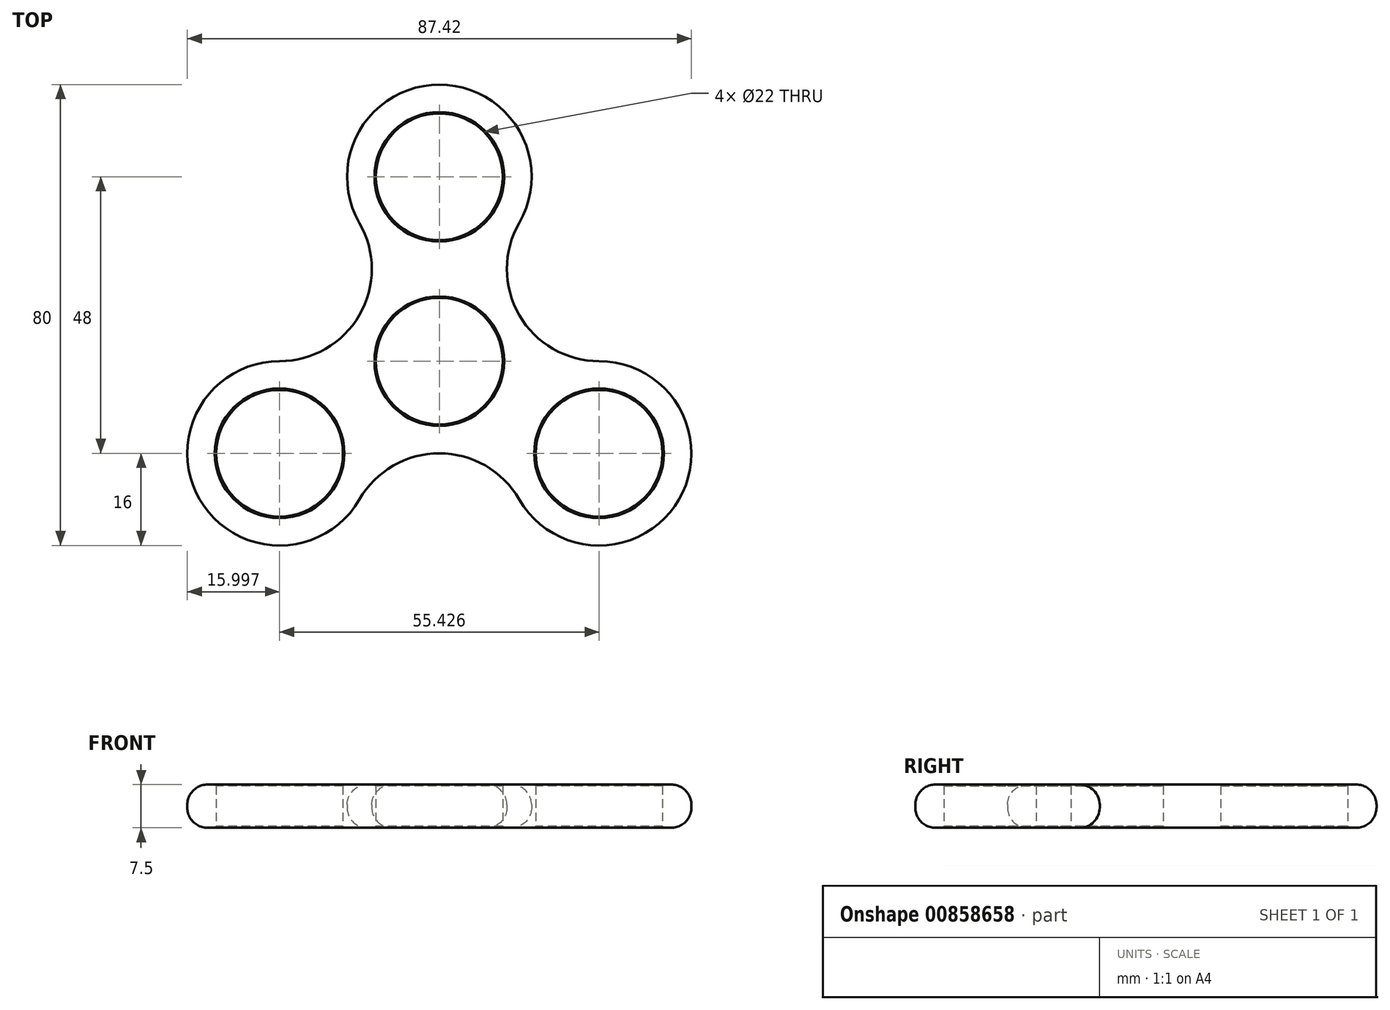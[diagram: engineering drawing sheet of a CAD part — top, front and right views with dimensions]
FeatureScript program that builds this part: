
annotation { "Feature Type Name" : "Feature", "Feature Type Description" : "" }
export const myFeature = defineFeature(function(context is Context, id is Id, definition is map)
    precondition{}
    {
        {
            var Q0;
            Q0=qCreatedBy(makeId("Top.planeOp"),FACE);
            var sketch = newSketch(context, id + "F0", { "sketchPlane" : qUnion([Q0])});
            skCircle(sketch, "E0", {"center": v(0, 0) * mm, "radius": 11 * mm});
            skLineSegment(sketch, "E1", {"start": v(0, 0) * mm, "end": v(0, 21) * mm});
            skLineSegment(sketch, "E2", {"start": v(0, 21) * mm, "end": v(0, 32) * mm});
            skCircle(sketch, "E3", {"center": v(0, 32) * mm, "radius": 11 * mm});
            skArc(sketch, "E4", {"start": v(13.86, 24) * mm, "mid": v(0, 48) * mm, "end": v(-13.86, 24) * mm});
            skArc(sketch, "E5.1.0", {"start": v(-27.71, 0) * mm, "mid": v(-41.57, -24) * mm, "end": v(-13.86, -24) * mm});
            skCircle(sketch, "E5.1.1", {"center": v(-27.71, -16) * mm, "radius": 11 * mm});
            skArc(sketch, "E5.2.0", {"start": v(13.86, -24) * mm, "mid": v(41.57, -24) * mm, "end": v(27.71, 0) * mm});
            skCircle(sketch, "E5.2.1", {"center": v(27.71, -16) * mm, "radius": 11 * mm});
            skArc(sketch, "E6", {"start": v(13.86, 24) * mm, "mid": v(13.86, 8) * mm, "end": v(27.71, 0) * mm});
            skArc(sketch, "E7.1.0", {"start": v(-27.71, 0) * mm, "mid": v(-13.86, 8) * mm, "end": v(-13.86, 24) * mm});
            skArc(sketch, "E7.2.0", {"start": v(13.86, -24) * mm, "mid": v(0, -16) * mm, "end": v(-13.86, -24) * mm});
            skSolve(sketch);
        }
        {
            var Q0;
            Q0=makeQuery(id+"F0.imprint","IMPRINT",FACE,{"disambiguationData":[TD([[makeQuery(id+"F0.imprint","IMPRINT",EDGE,{"derivedFrom":sQuery(id+"F0.wireOp",EDGE,"E0")}),-1.0]])]});
            extrude(context, id + "F1", {"entities" : qUnion([Q0]), "depth" : 7.5 * mm, "offsetDistance" : 25 * mm});
        }
        {
            var Q0;
            Q0=makeQuery(id+"F1.opExtrude","CAP_EDGE",EDGE,{"disambiguationData":[OSD([sQuery(id+"F0.wireOp",EDGE,"E5.1.0")])],"isStart":false});
            var Q1;
            Q1=makeQuery(id+"F1.opExtrude","CAP_EDGE",EDGE,{"disambiguationData":[OSD([sQuery(id+"F0.wireOp",EDGE,"E7.2.0")])],"isStart":true});
            fillet(context, id + "F2", {"entities" : qUnion([Q0, Q1]), "radius" : 3.5 * mm, "tangentPropagation" : true, "allowEdgeOverflow" : false});
        }
        {
            var Q0;
            Q0=makeQuery(id+"F1.opExtrude","CAP_EDGE",EDGE,{"disambiguationData":[OSD([sQuery(id+"F0.wireOp",EDGE,"E3")])],"isStart":false});
            var Q1;
            Q1=makeQuery(id+"F1.opExtrude","CAP_EDGE",EDGE,{"disambiguationData":[OSD([sQuery(id+"F0.wireOp",EDGE,"E0")])],"isStart":false});
            var Q2;
            Q2=makeQuery(id+"F1.opExtrude","CAP_EDGE",EDGE,{"disambiguationData":[OSD([sQuery(id+"F0.wireOp",EDGE,"E5.1.1")])],"isStart":false});
            var Q3;
            Q3=makeQuery(id+"F1.opExtrude","CAP_EDGE",EDGE,{"disambiguationData":[OSD([sQuery(id+"F0.wireOp",EDGE,"E5.2.1")])],"isStart":false});
            var Q4;
            Q4=makeQuery(id+"F1.opExtrude","CAP_EDGE",EDGE,{"disambiguationData":[OSD([sQuery(id+"F0.wireOp",EDGE,"E5.2.1")])],"isStart":true});
            var Q5;
            Q5=makeQuery(id+"F1.opExtrude","CAP_EDGE",EDGE,{"disambiguationData":[OSD([sQuery(id+"F0.wireOp",EDGE,"E0")])],"isStart":true});
            var Q6;
            Q6=makeQuery(id+"F1.opExtrude","CAP_EDGE",EDGE,{"disambiguationData":[OSD([sQuery(id+"F0.wireOp",EDGE,"E5.1.1")])],"isStart":true});
            var Q7;
            Q7=makeQuery(id+"F1.opExtrude","CAP_EDGE",EDGE,{"disambiguationData":[OSD([sQuery(id+"F0.wireOp",EDGE,"E3")])],"isStart":true});
            chamfer(context, id + "F3", {"entities" : qUnion([Q0, Q1, Q2, Q3, Q4, Q5, Q6, Q7]), "width" : .25 * mm, "tangentPropagation" : true});
        }
    });
